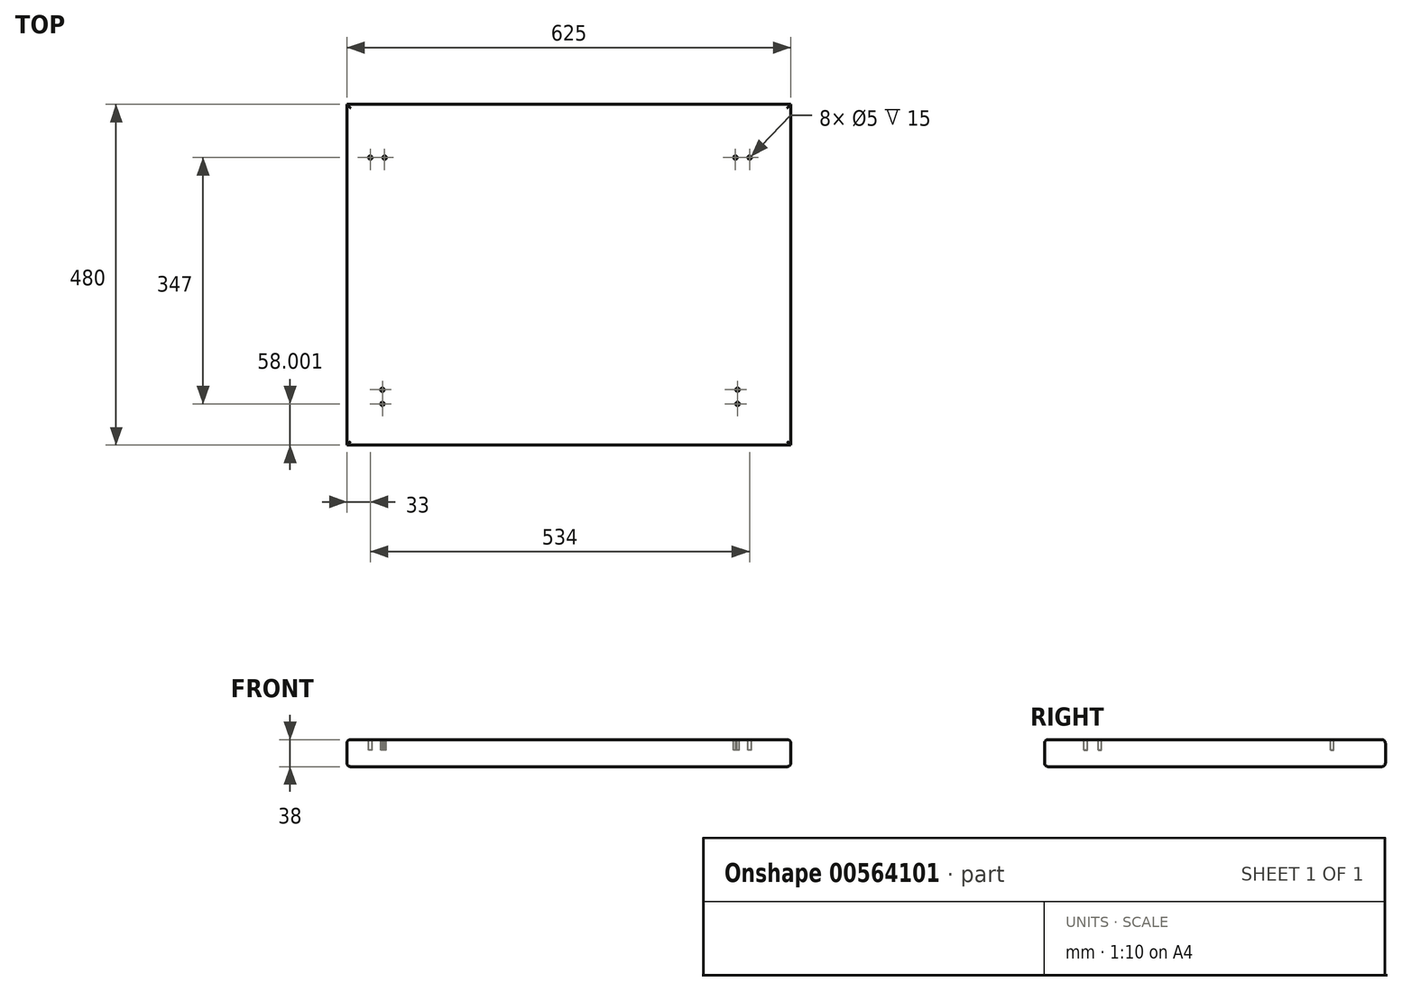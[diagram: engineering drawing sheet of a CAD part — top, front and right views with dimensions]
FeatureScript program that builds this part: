
annotation { "Feature Type Name" : "Feature", "Feature Type Description" : "" }
export const myFeature = defineFeature(function(context is Context, id is Id, definition is map)
    precondition{}
    {
        {
            var Q0;
            Q0=qCreatedBy(makeId("Top.planeOp"),FACE);
            var sketch = newSketch(context, id + "F0", { "sketchPlane" : qUnion([Q0])});
            skLineSegment(sketch, "E0.bottom", {"start": v(-308.85, 382.61) * mm, "end": v(316.15, 382.61) * mm});
            skLineSegment(sketch, "E0.top", {"start": v(-308.85, -97.39) * mm, "end": v(316.15, -97.39) * mm});
            skLineSegment(sketch, "E0.left", {"start": v(-308.85, 382.61) * mm, "end": v(-308.85, -97.39) * mm});
            skLineSegment(sketch, "E0.right", {"start": v(316.15, 382.61) * mm, "end": v(316.15, -97.39) * mm});
            skSolve(sketch);
        }
        {
            var Q0;
            Q0 = qSketchRegion(id + "F0", true);
            extrude(context, id + "F1", {"entities" : qUnion([Q0]), "depth" : 38 * mm, "offsetDistance" : 25 * mm});
        }
        {
            var Q0;
            Q0=makeQuery(id+"F1.opExtrude","CAP_FACE",FACE,{"disambiguationData":[OSD([sQuery(id+"F0.wireOp",EDGE,"E0.bottom"),sQuery(id+"F0.wireOp",EDGE,"E0.top"),sQuery(id+"F0.wireOp",EDGE,"E0.left"),sQuery(id+"F0.wireOp",EDGE,"E0.right")])],"isStart":false});
            var Q1;
            Q1=makeQuery(id+"F1.opExtrude","CAP_FACE",FACE,{"disambiguationData":[OSD([sQuery(id+"F0.wireOp",EDGE,"E0.bottom"),sQuery(id+"F0.wireOp",EDGE,"E0.top"),sQuery(id+"F0.wireOp",EDGE,"E0.left"),sQuery(id+"F0.wireOp",EDGE,"E0.right")])],"isStart":true});
            fillet(context, id + "F2", {"entities" : qUnion([Q0, Q1]), "radius" : 5 * mm, "tangentPropagation" : true, "allowEdgeOverflow" : false});
        }
        {
            var Q0;
            Q0=makeQuery(id+"F1.opExtrude","CAP_FACE",FACE,{"disambiguationData":[OSD([sQuery(id+"F0.wireOp",EDGE,"E0.bottom"),sQuery(id+"F0.wireOp",EDGE,"E0.top"),sQuery(id+"F0.wireOp",EDGE,"E0.left"),sQuery(id+"F0.wireOp",EDGE,"E0.right")])],"isStart":false});
            var sketch = newSketch(context, id + "F3", { "sketchPlane" : qUnion([Q0])});
            skCircle(sketch, "E1", {"center": v(-275.85, 307.61) * mm, "radius": 2.5 * mm});
            skCircle(sketch, "E2", {"center": v(-255.85, 307.61) * mm, "radius": 2.5 * mm});
            skCircle(sketch, "E3", {"center": v(-258.85, -39.39) * mm, "radius": 2.5 * mm});
            skCircle(sketch, "E4", {"center": v(-258.85, -19.39) * mm, "radius": 2.5 * mm});
            skCircle(sketch, "E5", {"center": v(238.15, 307.61) * mm, "radius": 2.5 * mm});
            skCircle(sketch, "E6", {"center": v(258.15, 307.61) * mm, "radius": 2.5 * mm});
            skCircle(sketch, "E7", {"center": v(241.15, -19.39) * mm, "radius": 2.5 * mm});
            skCircle(sketch, "E8", {"center": v(241.15, -39.39) * mm, "radius": 2.5 * mm});
            skSolve(sketch);
        }
        {
            var Q0;
            Q0 = qSketchRegion(id + "F3", true);
            extrude(context, id + "F4", {"entities" : qUnion([Q0]), "operationType" : NewBodyOperationType.REMOVE, "oppositeDirection" : true, "depth" : 15 * mm, "offsetDistance" : 25 * mm});
        }
    });
